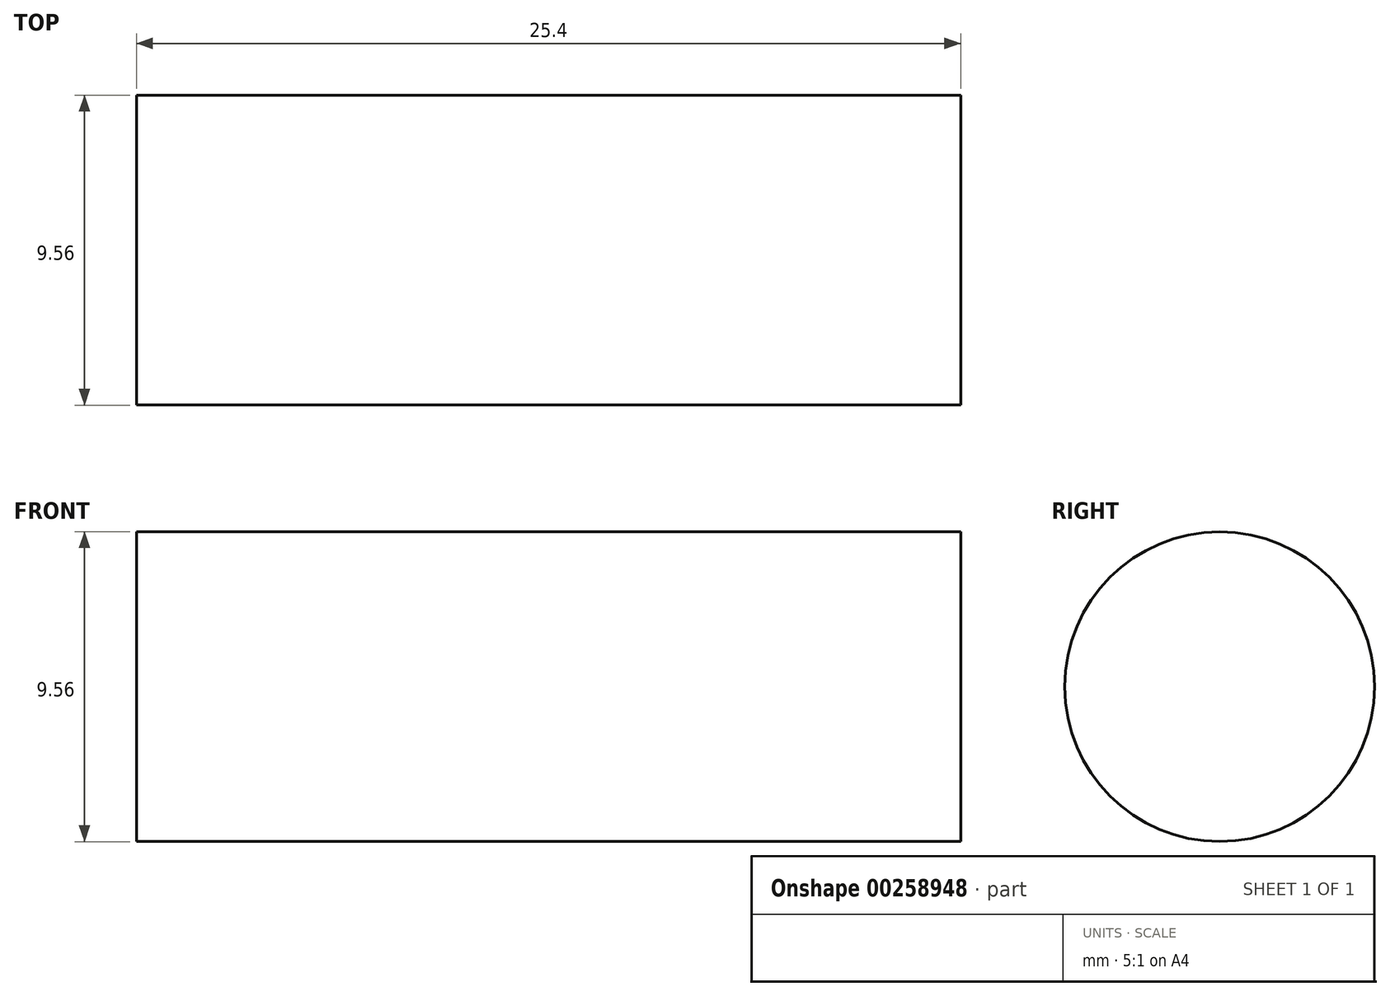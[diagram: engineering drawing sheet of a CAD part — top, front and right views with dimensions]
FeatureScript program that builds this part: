
annotation { "Feature Type Name" : "Feature", "Feature Type Description" : "" }
export const myFeature = defineFeature(function(context is Context, id is Id, definition is map)
    precondition{}
    {
        {
            var Q0;
            Q0=qCreatedBy(makeId("Front.planeOp"),FACE);
            var sketch = newSketch(context, id + "F0", { "sketchPlane" : qUnion([Q0])});
            skLineSegment(sketch, "E0.bottom", {"start": v(0, 0) * mm, "end": v(-25.4, 0) * mm});
            skLineSegment(sketch, "E0.top", {"start": v(0, -4.78) * mm, "end": v(-25.4, -4.78) * mm});
            skLineSegment(sketch, "E0.left", {"start": v(0, 0) * mm, "end": v(0, -4.78) * mm});
            skLineSegment(sketch, "E0.right", {"start": v(-25.4, 0) * mm, "end": v(-25.4, -4.78) * mm});
            skSolve(sketch);
        }
        {
            var Q0;
            Q0=makeQuery(id+"F0.imprint","IMPRINT",FACE,{"disambiguationData":[TD([[makeQuery(id+"F0.imprint","IMPRINT",EDGE,{"derivedFrom":sQuery(id+"F0.wireOp",EDGE,"E0.bottom")}),1.0]])]});
            var Q1;
            Q1=sQuery(id+"F0.wireOp",EDGE,"E0.bottom");
            revolve(context, id + "F1", {"entities" : qUnion([Q0]), "axis" : qUnion([Q1]), "revolveType" : RevolveType.FULL});
        }
    });
